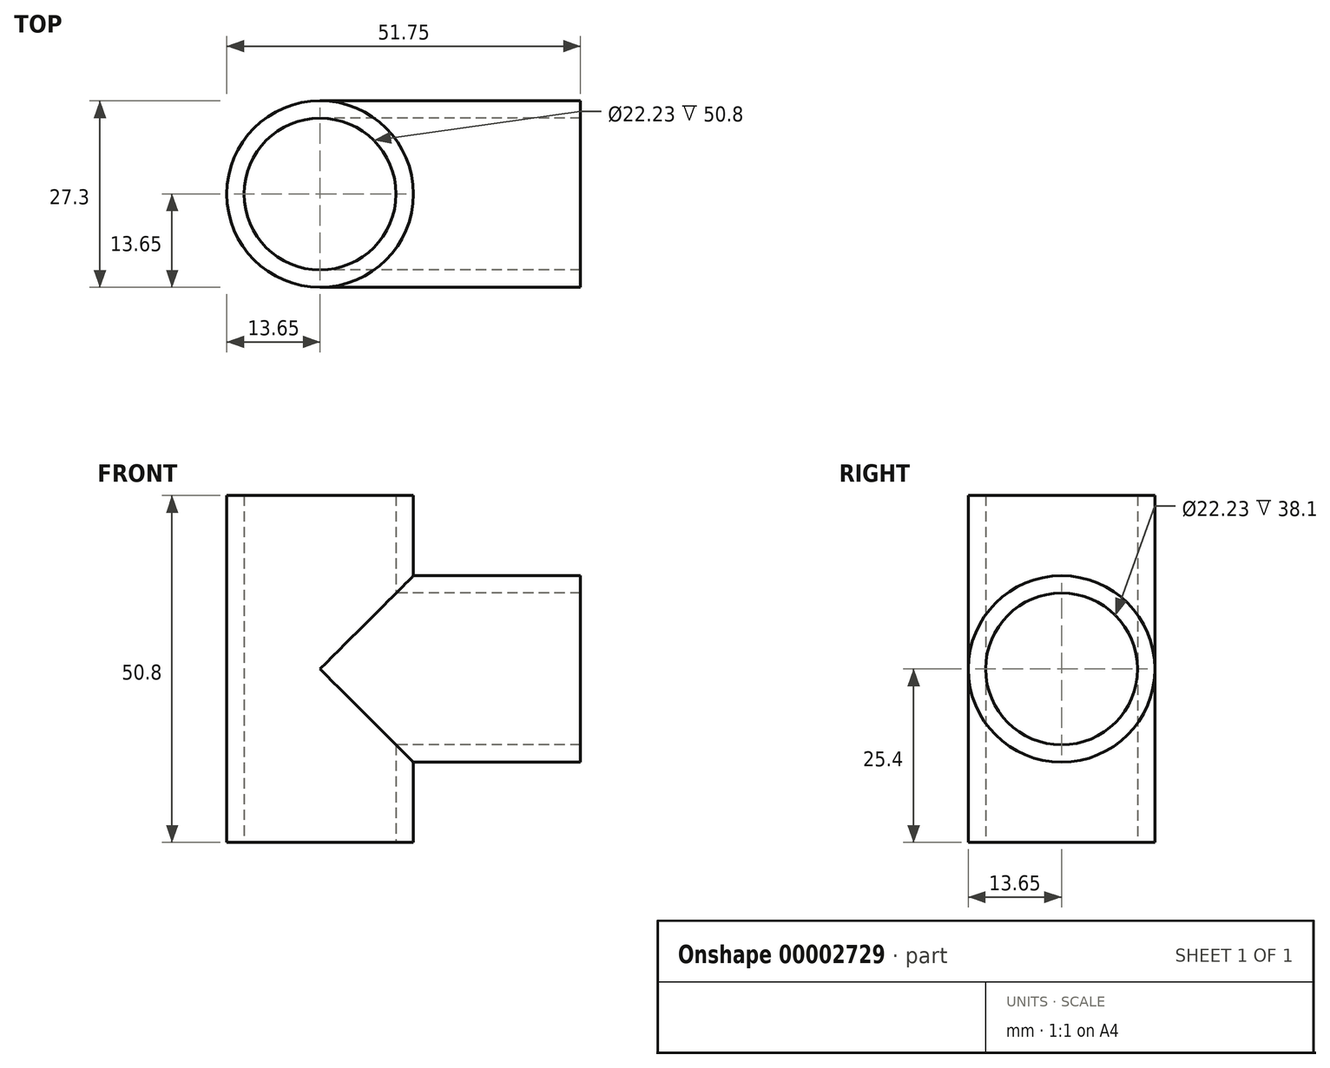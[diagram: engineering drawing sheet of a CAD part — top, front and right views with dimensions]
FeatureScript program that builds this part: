
annotation { "Feature Type Name" : "Feature", "Feature Type Description" : "" }
export const myFeature = defineFeature(function(context is Context, id is Id, definition is map)
    precondition{}
    {
        {
            var Q0;
            Q0=qCreatedBy(makeId("Top.planeOp"),FACE);
            var sketch = newSketch(context, id + "F0", { "sketchPlane" : qUnion([Q0])});
            skCircle(sketch, "E0", {"center": v(0, 0) * mm, "radius": 13.65 * mm});
            skSolve(sketch);
        }
        {
            var Q0;
            Q0=makeQuery(id+"F0.imprint","IMPRINT",FACE,{"disambiguationData":[TD([[makeQuery(id+"F0.imprint","IMPRINT",EDGE,{"derivedFrom":sQuery(id+"F0.wireOp",EDGE,"E0")}),1.0]])]});
            extrude(context, id + "F1", {"entities" : qUnion([Q0]), "depth" : 50.8 * mm});
        }
        {
            var Q0;
            Q0=qCreatedBy(makeId("Right.planeOp"),FACE);
            var sketch = newSketch(context, id + "F2", { "sketchPlane" : qUnion([Q0])});
            skLineSegment(sketch, "E1", {"start": v(0, 0) * mm, "end": v(0, 50.8) * mm, "construction": true});
            skSolve(sketch);
        }
        {
            var Q0;
            Q0=qCreatedBy(makeId("Right.planeOp"),FACE);
            var sketch = newSketch(context, id + "F3", { "sketchPlane" : qUnion([Q0])});
            skCircle(sketch, "E2", {"center": v(0, 25.4) * mm, "radius": 13.65 * mm});
            skSolve(sketch);
        }
        {
            var Q0;
            Q0=makeQuery(id+"F3.imprint","IMPRINT",FACE,{"disambiguationData":[TD([[makeQuery(id+"F3.imprint","IMPRINT",EDGE,{"derivedFrom":sQuery(id+"F3.wireOp",EDGE,"E2")}),1.0]])]});
            extrude(context, id + "F4", {"entities" : qUnion([Q0]), "operationType" : NewBodyOperationType.ADD, "depth" : 38.1 * mm});
        }
        {
            var Q0;
            Q0=makeQuery(id+"F4.opExtrude","CAP_FACE",FACE,{"disambiguationData":[OSD([sQuery(id+"F3.wireOp",EDGE,"E2")])],"isStart":false});
            var Q1;
            Q1=makeQuery(id+"F1.opExtrude","CAP_FACE",FACE,{"disambiguationData":[OSD([sQuery(id+"F0.wireOp",EDGE,"E0")])],"isStart":false});
            var Q2;
            Q2=makeQuery(id+"F1.opExtrude","CAP_FACE",FACE,{"disambiguationData":[OSD([sQuery(id+"F0.wireOp",EDGE,"E0")])],"isStart":true});
            shell(context, id + "F5", {"entities" : qUnion([Q0, Q1, Q2]), "thickness" : 2.54 * mm});
        }
    });
